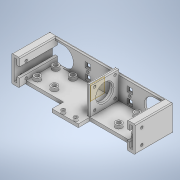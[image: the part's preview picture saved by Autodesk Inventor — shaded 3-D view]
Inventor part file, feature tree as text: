
AUTODESK INVENTOR PART (.ipt)
format: ipt  version: 2022 (Build 260153000, 153)  size: 501,760 bytes
history: native  units: in
note: dims shown in document units (in); Inventor stores cm internally (conversion verified against a paired STEP export)
features: sketch x20, extrude x17, mirror x3, fillet x1, plane x1, chamfer x1
ambient origin geometry x8: Origin, YZ Plane, XZ Plane, XY Plane, X Axis, Y Axis, Z Axis, Center Point
bodies: Solid1 (feature_tree)
feature tree (43):
  extrude  "Extrusion1"  Depth=1.8898in
  extrude  "Extrusion2"  Depth=0.1575in
  extrude  "Extrusion3"  Depth=0.1575in
  extrude  "Extrusion4"  Depth=0.1575in
  extrude  "Extrusion5"  Depth=0.1575in
  extrude  "Extrusion6"  Depth=0.315in TaperAngle=0.0deg
  extrude  "Extrusion7"  Depth=0.6102in
  sketch  "Sketch8"  dims[d19=0.315in d20=0.0in d21=0.1575in]
  extrude  "Extrusion8"  Depth=0.1575in
  extrude  "Extrusion9"  Depth=0.3937in TaperAngle=0.0deg
  extrude  "Extrusion10"  Depth=0.2362in
  sketch  "Sketch12"  dims[d29=0.3937in d30=0.0in d31=0.1969in]
  sketch  "Sketch13"  dims[d32=2.9528in d33=1.6654in d34=0.0in]
  extrude  "Extrusion14"  Depth=0.2362in
  mirror  "Mirror2"
  extrude  "Extrusion15"  Depth=0.1969in
  extrude  "Extrusion16"  Depth=1.6654in TaperAngle=0.0deg
  extrude  "Extrusion17"  Depth=0.1575in
  extrude  "Extrusion18"  Depth=0.1575in
  mirror  "Mirror3"
  extrude  "Extrusion19"  Depth=1.6654in TaperAngle=0.0deg
  mirror  "Mirror4"
  fillet  "Fillet1"  Radius=0.3937in
  plane  "Work Plane1"
  extrude  "Extrusion21"  Depth=0.3937in
  chamfer  "Chamfer1"  Distance=0.1969in
  sketch  "Sketch1"  dims[d0=7.4016in d1=1.8898in]
  sketch  "Sketch2"  dims[d2=0.1969in d3=0.0in d4=0.1575in]
  sketch  "Sketch3"  dims[d5=0.1575in d6=0.1575in]
  sketch  "Sketch4"  dims[d7=1.378in d8=0.0in d9=0.1575in]
  sketch  "Sketch5"  dims[d10=0.315in d11=0.0in d12=0.1575in]
  sketch  "Sketch6"  dims[d13=0.315in d14=0.0in d15=0.315in d16=0.0in]
  sketch  "Sketch7"  dims[d17=0.4921in d18=0.6102in]
  sketch  "Sketch9"  dims[d22=0.1575in d23=0.3937in d24=0.0in]
  sketch  "Sketch10"  dims[d25=0.2362in d26=0.2362in]
  sketch  "Sketch11"  dims[d27=0.2362in d28=0.2362in]
  sketch  "Sketch17"  dims[d35=0.1575in d36=0.1575in]
  sketch  "Sketch18"  dims[d37=0.1575in d38=0.1575in]
  sketch  "Sketch19"  dims[d39=0.9843in d40=1.6654in d41=0.0in d54=0.3937in]
  sketch  "Sketch20"  dims[d55=0.3937in d56=0.3937in]
  sketch  "Sketch21"  dims[d57=0.3937in d58=0.1969in d59=0.0in]
  sketch  "Sketch22"  dims[d60=1.5748in]
  sketch  "Sketch24"  dims[d61=0.1969in d62=0.689in d63=0.0in d64=0.1575in d65=0.1575in d66=0.689in d67=0.0in d68=0.2362in d69=0.2362in d70=0.1575in d71=0.0in d72=0.1575in d73=0.1575in d74=0.3937in d75=0.3937in d76=0.7874in d77=0.0in d78=0.315in d79=0.315in d80=0.315in d81=0.315in d82=0.1575in d83=0.7874in d84=0.0in d85=0.0591in d92=0.2362in d93=0.2362in d94=0.2362in d95=0.2362in d96=0.1181in d97=0.0in d98=1.4429in d99=0.2224in d100=0.2224in d101=1.4429in d102=0.8327in d103=0.1969in d104=0.2224in d105=0.2224in d106=0.8327in d107=1.4429in d108=1.4429in d109=0.0984in d110=0.0787in d111=45.0deg]
